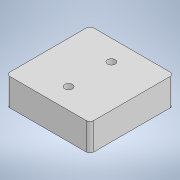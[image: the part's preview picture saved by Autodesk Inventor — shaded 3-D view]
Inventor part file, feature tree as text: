
AUTODESK INVENTOR PART (.ipt)
format: ipt  version: 2022 (Build 260153000, 153)  size: 117,248 bytes
history: native  units: mm
features: extrude x3, sketch x3, fillet x1
ambient origin geometry x8: Origin, YZ Plane, XZ Plane, XY Plane, X Axis, Y Axis, Z Axis, Center Point
bodies: Solid1 (feature_tree)
feature tree (7):
  extrude  "Extrusion1"  Depth=43.1mm
  extrude  "Extrusion2"  Depth=40.1mm
  fillet  "Fillet1"  Radius=40.1mm
  extrude  "Extrusion3"  Depth=2.0mm
  sketch  "Sketch1"  dims[d0=43.1mm d1=43.1mm]
  sketch  "Sketch2"  dims[d2=14.0mm d3=0.0mm d4=40.1mm d5=40.1mm]
  sketch  "Sketch3"  dims[d6=8.0mm d7=0.0mm d8=2.0mm d9=4.0mm d10=22.0mm d11=0.0mm d12=0.0mm]
